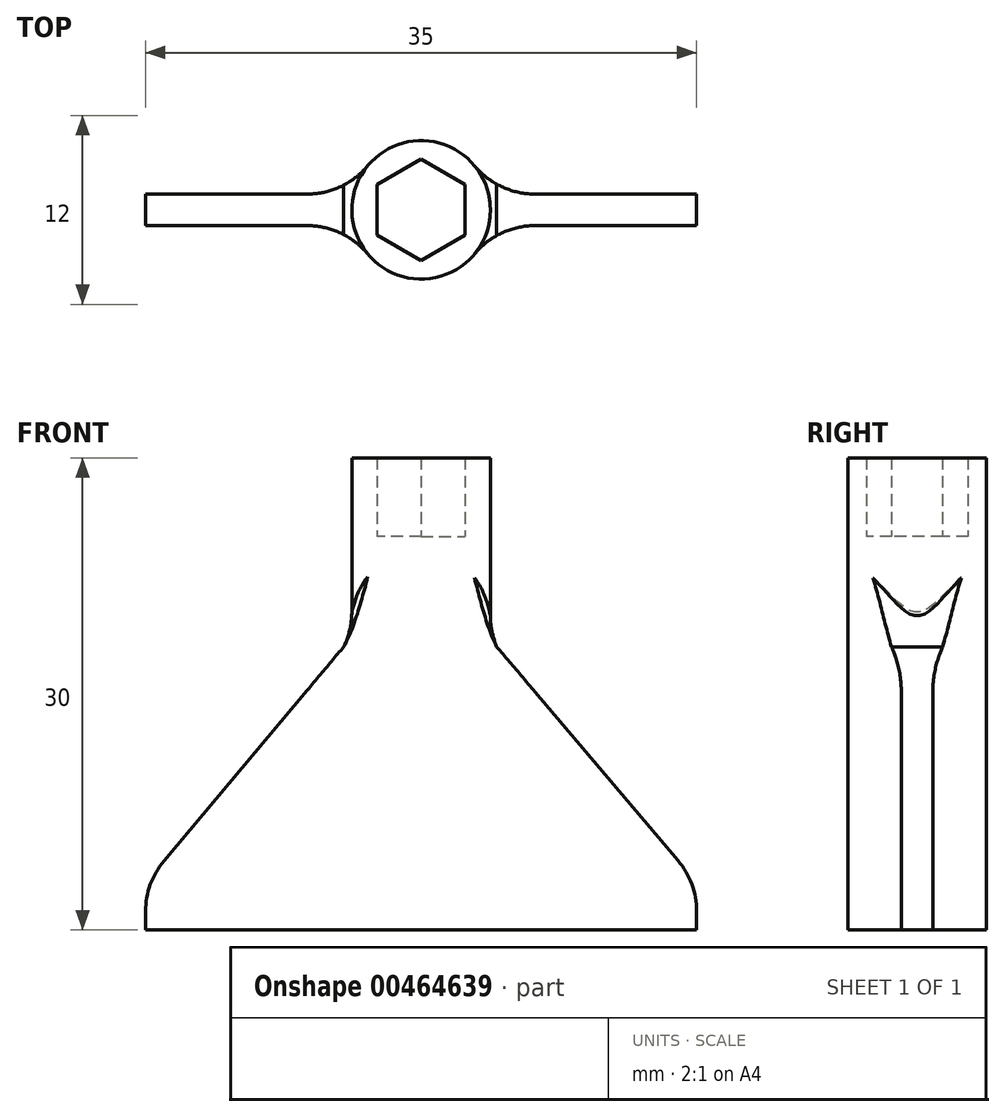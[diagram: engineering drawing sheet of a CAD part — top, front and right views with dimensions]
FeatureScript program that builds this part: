
annotation { "Feature Type Name" : "Feature", "Feature Type Description" : "" }
export const myFeature = defineFeature(function(context is Context, id is Id, definition is map)
    precondition{}
    {
        {
            var Q0;
            Q0=qCreatedBy(makeId("Top.planeOp"),FACE);
            var sketch = newSketch(context, id + "F0", { "sketchPlane" : qUnion([Q0])});
            skCircle(sketch, "E0", {"center": v(0, 0) * mm, "radius": 4.4 * mm});
            skCircle(sketch, "E1.cCircle", {"center": v(0, 0) * mm, "radius": 2.8 * mm, "construction": true});
            skLineSegment(sketch, "E1.0", {"start": v(2.8, 1.62) * mm, "end": v(2.8, -1.62) * mm});
            skLineSegment(sketch, "E1.1", {"start": v(2.8, -1.62) * mm, "end": v(0, -3.23) * mm});
            skLineSegment(sketch, "E1.2", {"start": v(0, -3.23) * mm, "end": v(-2.8, -1.62) * mm});
            skLineSegment(sketch, "E1.3", {"start": v(-2.8, -1.62) * mm, "end": v(-2.8, 1.62) * mm});
            skLineSegment(sketch, "E1.4", {"start": v(-2.8, 1.62) * mm, "end": v(0, 3.23) * mm});
            skLineSegment(sketch, "E1.5", {"start": v(0, 3.23) * mm, "end": v(2.8, 1.62) * mm});
            skPoint(sketch, "E1.0.midPoint", {"position": v(2.8, 0) * mm});
            skSolve(sketch);
        }
        {
            var Q0;
            Q0 = qSketchRegion(id + "F0", true);
            extrude(context, id + "F1", {"entities" : qUnion([Q0]), "depth" : 5 * mm});
        }
        {
            var Q0;
            Q0=makeQuery(id+"F1.opExtrude","CAP_FACE",FACE,{"disambiguationData":[OSD([sQuery(id+"F0.wireOp",EDGE,"E0"),sQuery(id+"F0.wireOp",EDGE,"E1.0"),sQuery(id+"F0.wireOp",EDGE,"E1.1"),sQuery(id+"F0.wireOp",EDGE,"E1.2"),sQuery(id+"F0.wireOp",EDGE,"E1.3"),sQuery(id+"F0.wireOp",EDGE,"E1.4"),sQuery(id+"F0.wireOp",EDGE,"E1.5")])],"isStart":true});
            var sketch = newSketch(context, id + "F2", { "sketchPlane" : qUnion([Q0])});
            skCircle(sketch, "E2", {"center": v(0, 0) * mm, "radius": 4.4 * mm});
            skSolve(sketch);
        }
        {
            var Q0;
            Q0 = qSketchRegion(id + "F2", true);
            extrude(context, id + "F3", {"entities" : qUnion([Q0]), "operationType" : NewBodyOperationType.ADD, "depth" : 25 * mm});
        }
        {
            var Q0;
            Q0=makeQuery(id+"F3.opExtrude","CAP_FACE",FACE,{"disambiguationData":[OSD([sQuery(id+"F2.wireOp",EDGE,"E2")])],"isStart":false});
            var sketch = newSketch(context, id + "F4", { "sketchPlane" : qUnion([Q0])});
            skLineSegment(sketch, "E3.bottom", {"start": v(-17.5, 1) * mm, "end": v(17.5, 1) * mm});
            skLineSegment(sketch, "E3.top", {"start": v(-17.5, -1) * mm, "end": v(17.5, -1) * mm});
            skLineSegment(sketch, "E3.left", {"start": v(-17.5, 1) * mm, "end": v(-17.5, -1) * mm});
            skLineSegment(sketch, "E3.right", {"start": v(17.5, 1) * mm, "end": v(17.5, -1) * mm});
            skSolve(sketch);
        }
        {
            var Q0;
            Q0 = qSketchRegion(id + "F4", true);
            extrude(context, id + "F5", {"entities" : qUnion([Q0]), "operationType" : NewBodyOperationType.ADD, "oppositeDirection" : true, "depth" : 18 * mm});
        }
        {
            var Q0;
            Q0=makeQuery(id+"F5.opExtrude","CAP_EDGE",EDGE,{"disambiguationData":[OSD([sQuery(id+"F4.wireOp",EDGE,"E3.left")])],"isStart":false});
            chamfer(context, id + "F6", {"entities" : qUnion([Q0]), "chamferType" : ChamferType.OFFSET_ANGLE, "width" : 15 * mm, "oppositeDirection" : false, "angle" : 40 * degree, "tangentPropagation" : true});
        }
        {
            var Q0;
            Q0=makeQuery(id+"F5.opExtrude","CAP_EDGE",EDGE,{"disambiguationData":[OSD([sQuery(id+"F4.wireOp",EDGE,"E3.right")])],"isStart":false});
            chamfer(context, id + "F7", {"entities" : qUnion([Q0]), "chamferType" : ChamferType.OFFSET_ANGLE, "width" : 12.7 * mm, "oppositeDirection" : false, "angle" : 49.7 * degree, "tangentPropagation" : true});
        }
        {
            var Q0;
            Q0=makeQuery(id+"F5.boolean.opBoolean","INTERSECT",EDGE,{"disambiguationData":[OD(0.0)],"derivedFrom":[makeQuery(id+"F3.boolean.opBoolean","MERGE",FACE,{"derivedFrom":[makeQuery(id+"F1.opExtrude","SWEPT_FACE",FACE,{"disambiguationData":[OSD([sQuery(id+"F0.wireOp",EDGE,"E0")])]}),makeQuery(id+"F3.opExtrude","SWEPT_FACE",FACE,{"disambiguationData":[OSD([sQuery(id+"F2.wireOp",EDGE,"E2")])]})]}),makeQuery(id+"F5.opExtrude","CAP_FACE",FACE,{"disambiguationData":[OSD([sQuery(id+"F4.wireOp",EDGE,"E3.bottom"),sQuery(id+"F4.wireOp",EDGE,"E3.top"),sQuery(id+"F4.wireOp",EDGE,"E3.left"),sQuery(id+"F4.wireOp",EDGE,"E3.right")])],"isStart":false})]});
            var Q1;
            Q1=makeQuery(id+"F5.boolean.opBoolean","INTERSECT",EDGE,{"disambiguationData":[OD(1.0)],"derivedFrom":[makeQuery(id+"F3.boolean.opBoolean","MERGE",FACE,{"derivedFrom":[makeQuery(id+"F1.opExtrude","SWEPT_FACE",FACE,{"disambiguationData":[OSD([sQuery(id+"F0.wireOp",EDGE,"E0")])]}),makeQuery(id+"F3.opExtrude","SWEPT_FACE",FACE,{"disambiguationData":[OSD([sQuery(id+"F2.wireOp",EDGE,"E2")])]})]}),makeQuery(id+"F5.opExtrude","CAP_FACE",FACE,{"disambiguationData":[OSD([sQuery(id+"F4.wireOp",EDGE,"E3.bottom"),sQuery(id+"F4.wireOp",EDGE,"E3.top"),sQuery(id+"F4.wireOp",EDGE,"E3.left"),sQuery(id+"F4.wireOp",EDGE,"E3.right")])],"isStart":false})]});
            fillet(context, id + "F8", {"entities" : qUnion([Q0, Q1]), "radius" : 5 * mm, "tangentPropagation" : true, "allowEdgeOverflow" : false});
        }
        {
            var Q0;
            {var subQ0=sQuery(id+"F4.wireOp",EDGE,"E3.right");Q0=makeQuery(id+"F7.opChamfer","BLEND_EDGE",EDGE,{"blendedFrom":[makeQuery(id+"F5.opExtrude","CAP_EDGE",EDGE,{"disambiguationData":[OSD([subQ0])],"isStart":false}),makeQuery(id+"F5.opExtrude","SWEPT_FACE",FACE,{"disambiguationData":[OSD([subQ0])]})],"blendedInto":[makeQuery(id+"F5.opExtrude","SWEPT_FACE",FACE,{"disambiguationData":[OSD([subQ0])]})]});}
            var Q1;
            {var subQ0=sQuery(id+"F4.wireOp",EDGE,"E3.left");Q1=makeQuery(id+"F6.opChamfer","BLEND_EDGE",EDGE,{"blendedFrom":[makeQuery(id+"F5.opExtrude","CAP_EDGE",EDGE,{"disambiguationData":[OSD([subQ0])],"isStart":false}),makeQuery(id+"F5.opExtrude","SWEPT_FACE",FACE,{"disambiguationData":[OSD([subQ0])]})],"blendedInto":[makeQuery(id+"F5.opExtrude","SWEPT_FACE",FACE,{"disambiguationData":[OSD([subQ0])]})]});}
            var Q2;
            Q2=makeQuery(id+"F5.boolean.opBoolean","INTERSECT",EDGE,{"disambiguationData":[OD(0.0)],"derivedFrom":[makeQuery(id+"F3.boolean.opBoolean","MERGE",FACE,{"derivedFrom":[makeQuery(id+"F1.opExtrude","SWEPT_FACE",FACE,{"disambiguationData":[OSD([sQuery(id+"F0.wireOp",EDGE,"E0")])]}),makeQuery(id+"F3.opExtrude","SWEPT_FACE",FACE,{"disambiguationData":[OSD([sQuery(id+"F2.wireOp",EDGE,"E2")])]})]}),makeQuery(id+"F5.opExtrude","SWEPT_FACE",FACE,{"disambiguationData":[OSD([sQuery(id+"F4.wireOp",EDGE,"E3.bottom")])]})]});
            var Q3;
            Q3=makeQuery(id+"F5.boolean.opBoolean","INTERSECT",EDGE,{"disambiguationData":[OD(0.0)],"derivedFrom":[makeQuery(id+"F3.boolean.opBoolean","MERGE",FACE,{"derivedFrom":[makeQuery(id+"F1.opExtrude","SWEPT_FACE",FACE,{"disambiguationData":[OSD([sQuery(id+"F0.wireOp",EDGE,"E0")])]}),makeQuery(id+"F3.opExtrude","SWEPT_FACE",FACE,{"disambiguationData":[OSD([sQuery(id+"F2.wireOp",EDGE,"E2")])]})]}),makeQuery(id+"F5.opExtrude","SWEPT_FACE",FACE,{"disambiguationData":[OSD([sQuery(id+"F4.wireOp",EDGE,"E3.top")])]})]});
            var Q4;
            Q4=makeQuery(id+"F5.boolean.opBoolean","INTERSECT",EDGE,{"disambiguationData":[OD(1.0)],"derivedFrom":[makeQuery(id+"F3.boolean.opBoolean","MERGE",FACE,{"derivedFrom":[makeQuery(id+"F1.opExtrude","SWEPT_FACE",FACE,{"disambiguationData":[OSD([sQuery(id+"F0.wireOp",EDGE,"E0")])]}),makeQuery(id+"F3.opExtrude","SWEPT_FACE",FACE,{"disambiguationData":[OSD([sQuery(id+"F2.wireOp",EDGE,"E2")])]})]}),makeQuery(id+"F5.opExtrude","SWEPT_FACE",FACE,{"disambiguationData":[OSD([sQuery(id+"F4.wireOp",EDGE,"E3.top")])]})]});
            var Q5;
            Q5=makeQuery(id+"F5.boolean.opBoolean","INTERSECT",EDGE,{"disambiguationData":[OD(1.0)],"derivedFrom":[makeQuery(id+"F3.boolean.opBoolean","MERGE",FACE,{"derivedFrom":[makeQuery(id+"F1.opExtrude","SWEPT_FACE",FACE,{"disambiguationData":[OSD([sQuery(id+"F0.wireOp",EDGE,"E0")])]}),makeQuery(id+"F3.opExtrude","SWEPT_FACE",FACE,{"disambiguationData":[OSD([sQuery(id+"F2.wireOp",EDGE,"E2")])]})]}),makeQuery(id+"F5.opExtrude","SWEPT_FACE",FACE,{"disambiguationData":[OSD([sQuery(id+"F4.wireOp",EDGE,"E3.bottom")])]})]});
            fillet(context, id + "F9", {"entities" : qUnion([Q0, Q1, Q2, Q3, Q4, Q5]), "radius" : 5 * mm, "tangentPropagation" : true, "allowEdgeOverflow" : false});
        }
    });
